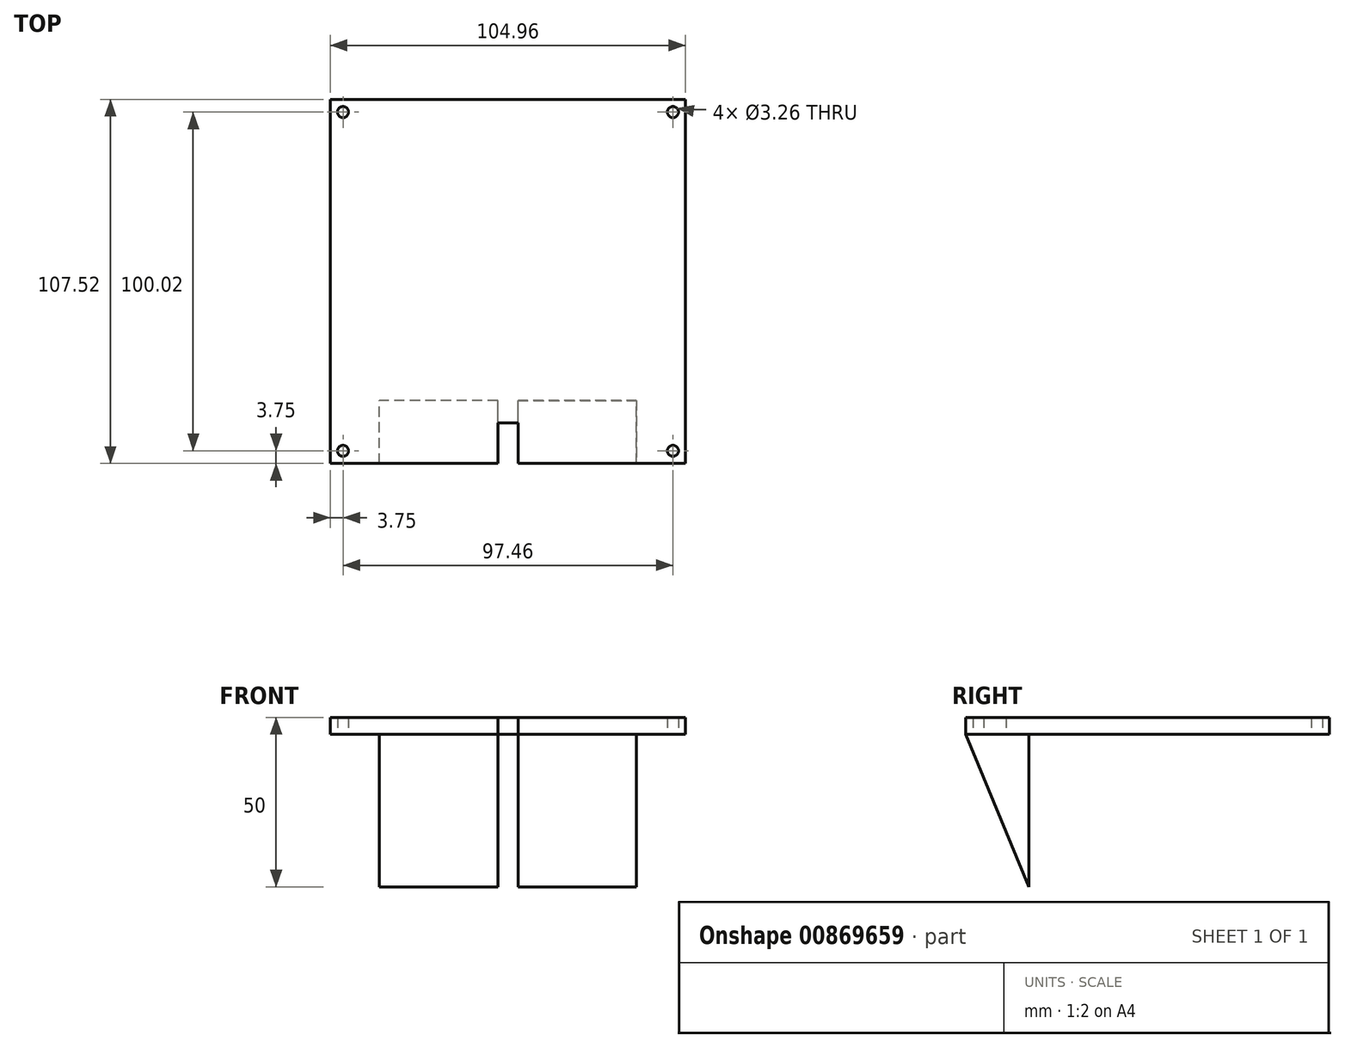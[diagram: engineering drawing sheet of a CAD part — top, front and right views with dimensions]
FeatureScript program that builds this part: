
annotation { "Feature Type Name" : "Feature", "Feature Type Description" : "" }
export const myFeature = defineFeature(function(context is Context, id is Id, definition is map)
    precondition{}
    {
        {
            var Q0;
            Q0=qCreatedBy(makeId("Top.planeOp"),FACE);
            var sketch = newSketch(context, id + "F0", { "sketchPlane" : qUnion([Q0])});
            skLineSegment(sketch, "E0.bottom", {"start": v(-52.48, -53.76) * mm, "end": v(52.48, -53.76) * mm});
            skLineSegment(sketch, "E0.top", {"start": v(-52.48, 53.76) * mm, "end": v(52.48, 53.76) * mm});
            skLineSegment(sketch, "E0.left", {"start": v(-52.48, -53.76) * mm, "end": v(-52.48, 53.76) * mm});
            skLineSegment(sketch, "E0.right", {"start": v(52.48, -53.76) * mm, "end": v(52.48, 53.76) * mm});
            skPoint(sketch, "E0.middle", {"position": v(0, 0) * mm});
            skCircle(sketch, "E1", {"center": v(-48.73, 50) * mm, "radius": 1.63 * mm});
            skCircle(sketch, "E2.MirrorC", {"center": v(48.73, 50) * mm, "radius": 1.63 * mm});
            skCircle(sketch, "E3.MirrorC", {"center": v(-48.73, -50) * mm, "radius": 1.63 * mm});
            skCircle(sketch, "E4.MirrorC", {"center": v(48.73, -50) * mm, "radius": 1.63 * mm});
            skLineSegment(sketch, "E5.bottom", {"start": v(-3, -53.76) * mm, "end": v(3, -53.76) * mm});
            skLineSegment(sketch, "E5.top", {"start": v(-3, -41.76) * mm, "end": v(3, -41.76) * mm});
            skLineSegment(sketch, "E5.left", {"start": v(-3, -53.76) * mm, "end": v(-3, -41.76) * mm});
            skLineSegment(sketch, "E5.right", {"start": v(3, -53.76) * mm, "end": v(3, -41.76) * mm});
            skSolve(sketch);
        }
        {
            var Q0;
            Q0=makeQuery(id+"F0.imprint","IMPRINT",FACE,{"disambiguationData":[TD([[makeQuery(id+"F0.imprint","IMPRINT",EDGE,{"derivedFrom":sQuery(id+"F0.wireOp",EDGE,"E0.bottom")}),1.0]])]});
            extrude(context, id + "F1", {"entities" : qUnion([Q0]), "depth" : 5 * mm, "offsetDistance" : 25 * mm});
        }
        {
            var Q0;
            Q0=makeQuery(id+"F1.opExtrude","CAP_FACE",FACE,{"disambiguationData":[OSD([sQuery(id+"F0.wireOp",EDGE,"E0.bottom"),sQuery(id+"F0.wireOp",EDGE,"E0.top"),sQuery(id+"F0.wireOp",EDGE,"E0.left"),sQuery(id+"F0.wireOp",EDGE,"E0.right"),sQuery(id+"F0.wireOp",EDGE,"E1"),sQuery(id+"F0.wireOp",EDGE,"E2.MirrorC"),sQuery(id+"F0.wireOp",EDGE,"E3.MirrorC"),sQuery(id+"F0.wireOp",EDGE,"E4.MirrorC"),sQuery(id+"F0.wireOp",EDGE,"E5.top"),sQuery(id+"F0.wireOp",EDGE,"E5.left"),sQuery(id+"F0.wireOp",EDGE,"E5.right")])],"isStart":false});
            var sketch = newSketch(context, id + "F2", { "sketchPlane" : qUnion([Q0])});
            skLineSegment(sketch, "E6.bottom", {"start": v(3, -53.76) * mm, "end": v(38, -53.76) * mm});
            skLineSegment(sketch, "E6.top", {"start": v(3, -35.12) * mm, "end": v(38, -35.12) * mm});
            skLineSegment(sketch, "E6.left", {"start": v(3, -53.76) * mm, "end": v(3, -35.12) * mm});
            skLineSegment(sketch, "E6.right", {"start": v(38, -53.76) * mm, "end": v(38, -35.12) * mm});
            skLineSegment(sketch, "E7.MirrorCS", {"start": v(-3, -53.76) * mm, "end": v(-3, -35.12) * mm});
            skLineSegment(sketch, "E8.MirrorCS", {"start": v(-3, -35.12) * mm, "end": v(-38, -35.12) * mm});
            skLineSegment(sketch, "E9.MirrorCS", {"start": v(-3, -53.76) * mm, "end": v(-38, -53.76) * mm});
            skLineSegment(sketch, "E10.MirrorCS", {"start": v(-38, -53.76) * mm, "end": v(-38, -35.12) * mm});
            skSolve(sketch);
        }
        {
            var Q0;
            Q0 = qSketchRegion(id + "F2", true);
            extrude(context, id + "F3", {"entities" : qUnion([Q0]), "operationType" : NewBodyOperationType.ADD, "oppositeDirection" : true, "depth" : 50 * mm, "offsetDistance" : 25 * mm});
        }
        {
            var Q0;
            Q0=makeQuery(id+"F3.opExtrude","SWEPT_FACE",FACE,{"disambiguationData":[OSD([sQuery(id+"F2.wireOp",EDGE,"E10.MirrorCS")])]});
            var sketch = newSketch(context, id + "F4", { "sketchPlane" : qUnion([Q0])});
            skLineSegment(sketch, "E11", {"start": v(53.76, 0) * mm, "end": v(35.12, -45) * mm});
            skLineSegment(sketch, "E12", {"start": v(35.12, -45) * mm, "end": v(35.12, 0) * mm});
            skSolve(sketch);
        }
        {
            var Q0;
            {var subQ0=sQuery(id+"F4.wireOp",EDGE,"E11");Q0=makeQuery(id+"F4.imprint","IMPRINT",FACE,{"disambiguationData":[TD([[makeQuery(id+"F4.imprint","IMPRINT",EDGE,{"derivedFrom":subQ0}),1.0]])]});}
            extrude(context, id + "F5", {"entities" : qUnion([Q0]), "operationType" : NewBodyOperationType.REMOVE, "endBound" : BoundingType.THROUGH_ALL, "oppositeDirection" : true, "depth" : 25 * mm, "offsetDistance" : 25 * mm});
        }
    });
